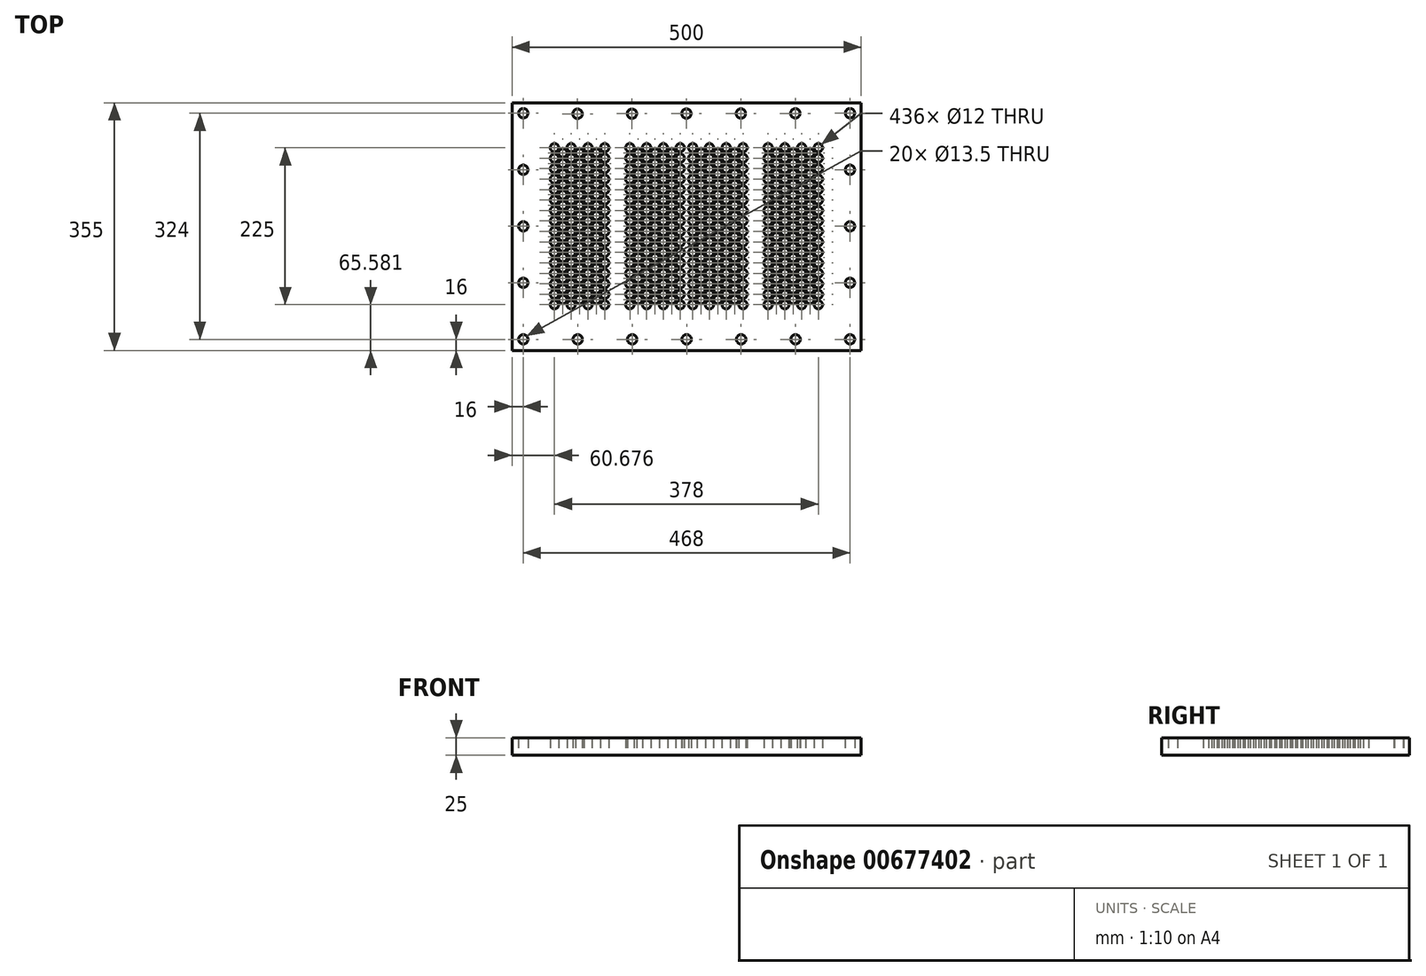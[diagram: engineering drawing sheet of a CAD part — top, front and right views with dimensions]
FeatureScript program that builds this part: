
annotation { "Feature Type Name" : "Feature", "Feature Type Description" : "" }
export const myFeature = defineFeature(function(context is Context, id is Id, definition is map)
    precondition{}
    {
        {
            var Q0;
            Q0=qCreatedBy(makeId("Top.planeOp"),FACE);
            var sketch = newSketch(context, id + "F0", { "sketchPlane" : qUnion([Q0])});
            skLineSegment(sketch, "E0", {"start": v(0, 0) * mm, "end": v(500, 0) * mm});
            skLineSegment(sketch, "E1", {"start": v(500, 0) * mm, "end": v(500, 355) * mm});
            skLineSegment(sketch, "E2", {"start": v(500, 355) * mm, "end": v(0, 355) * mm});
            skLineSegment(sketch, "E3", {"start": v(0, 355) * mm, "end": v(0, 0) * mm});
            skCircle(sketch, "E4", {"center": v(16, 16) * mm, "radius": 6.75 * mm});
            skCircle(sketch, "E5.1.0.0", {"center": v(94, 16) * mm, "radius": 6.75 * mm});
            skCircle(sketch, "E5.2.0.0", {"center": v(172, 16) * mm, "radius": 6.75 * mm});
            skCircle(sketch, "E5.3.0.0", {"center": v(250, 16) * mm, "radius": 6.75 * mm});
            skCircle(sketch, "E5.4.0.0", {"center": v(328, 16) * mm, "radius": 6.75 * mm});
            skCircle(sketch, "E5.5.0.0", {"center": v(406, 16) * mm, "radius": 6.75 * mm});
            skCircle(sketch, "E5.6.0.0", {"center": v(484, 16) * mm, "radius": 6.75 * mm});
            skCircle(sketch, "E6.0.1.0", {"center": v(16, 97) * mm, "radius": 6.75 * mm});
            skCircle(sketch, "E6.0.1.1", {"center": v(484, 97) * mm, "radius": 6.75 * mm});
            skCircle(sketch, "E6.0.2.0", {"center": v(16, 178) * mm, "radius": 6.75 * mm});
            skCircle(sketch, "E6.0.2.1", {"center": v(484, 178) * mm, "radius": 6.75 * mm});
            skCircle(sketch, "E6.0.3.0", {"center": v(16, 259) * mm, "radius": 6.75 * mm});
            skCircle(sketch, "E6.0.3.1", {"center": v(484, 259) * mm, "radius": 6.75 * mm});
            skCircle(sketch, "E6.0.4.0", {"center": v(16, 340) * mm, "radius": 6.75 * mm});
            skCircle(sketch, "E6.0.4.1", {"center": v(484, 340) * mm, "radius": 6.75 * mm});
            skCircle(sketch, "E7.MirrorC", {"center": v(171.68, 339.34) * mm, "radius": 6.75 * mm});
            skCircle(sketch, "E8.MirrorC", {"center": v(93.68, 339.19) * mm, "radius": 6.75 * mm});
            skCircle(sketch, "E9.MirrorC", {"center": v(249.68, 339.5) * mm, "radius": 6.75 * mm});
            skCircle(sketch, "E10.MirrorC", {"center": v(327.68, 339.66) * mm, "radius": 6.75 * mm});
            skCircle(sketch, "E11.MirrorC", {"center": v(405.68, 339.81) * mm, "radius": 6.75 * mm});
            skLineSegment(sketch, "E12", {"start": v(249.68, 355) * mm, "end": v(249.68, 0) * mm, "construction": true});
            skLineSegment(sketch, "E13", {"start": v(0, 177.5) * mm, "end": v(500, 178) * mm, "construction": true});
            skCircle(sketch, "E14.0.1.0", {"center": v(438.68, 80.58) * mm, "radius": 6 * mm});
            skCircle(sketch, "E14.0.2.0", {"center": v(438.68, 95.58) * mm, "radius": 6 * mm});
            skCircle(sketch, "E14.0.3.0", {"center": v(438.68, 110.58) * mm, "radius": 6 * mm});
            skCircle(sketch, "E14.0.4.0", {"center": v(438.68, 125.58) * mm, "radius": 6 * mm});
            skCircle(sketch, "E14.0.5.0", {"center": v(438.68, 140.58) * mm, "radius": 6 * mm});
            skCircle(sketch, "E14.0.6.0", {"center": v(438.68, 155.58) * mm, "radius": 6 * mm});
            skCircle(sketch, "E14.0.7.0", {"center": v(438.68, 170.58) * mm, "radius": 6 * mm});
            skCircle(sketch, "E14.0.8.0", {"center": v(438.68, 185.58) * mm, "radius": 6 * mm});
            skCircle(sketch, "E14.0.9.0", {"center": v(438.68, 200.58) * mm, "radius": 6 * mm});
            skCircle(sketch, "E14.0.10.0", {"center": v(438.68, 215.58) * mm, "radius": 6 * mm});
            skCircle(sketch, "E14.0.11.0", {"center": v(438.68, 230.58) * mm, "radius": 6 * mm});
            skCircle(sketch, "E14.0.12.0", {"center": v(438.68, 245.58) * mm, "radius": 6 * mm});
            skCircle(sketch, "E14.0.13.0", {"center": v(438.68, 260.58) * mm, "radius": 6 * mm});
            skCircle(sketch, "E14.0.14.0", {"center": v(438.68, 275.58) * mm, "radius": 6 * mm});
            skCircle(sketch, "E14.0.15.0", {"center": v(438.68, 290.58) * mm, "radius": 6 * mm});
            skCircle(sketch, "E15.0.1.0", {"center": v(438.67, 65.58) * mm, "radius": 6 * mm});
            skCircle(sketch, "E16.1.0.0", {"center": v(414.68, 200.58) * mm, "radius": 6 * mm});
            skCircle(sketch, "E16.1.0.1", {"center": v(414.68, 185.58) * mm, "radius": 6 * mm});
            skCircle(sketch, "E16.1.0.2", {"center": v(414.68, 170.58) * mm, "radius": 6 * mm});
            skCircle(sketch, "E16.1.0.3", {"center": v(414.68, 155.58) * mm, "radius": 6 * mm});
            skCircle(sketch, "E16.1.0.4", {"center": v(414.68, 140.58) * mm, "radius": 6 * mm});
            skCircle(sketch, "E16.1.0.5", {"center": v(414.68, 110.58) * mm, "radius": 6 * mm});
            skCircle(sketch, "E16.1.0.6", {"center": v(414.68, 125.58) * mm, "radius": 6 * mm});
            skCircle(sketch, "E16.1.0.7", {"center": v(414.68, 95.58) * mm, "radius": 6 * mm});
            skCircle(sketch, "E16.1.0.8", {"center": v(414.68, 80.58) * mm, "radius": 6 * mm});
            skCircle(sketch, "E16.1.0.9", {"center": v(414.68, 65.58) * mm, "radius": 6 * mm});
            skCircle(sketch, "E16.1.0.10", {"center": v(414.68, 290.58) * mm, "radius": 6 * mm});
            skCircle(sketch, "E16.1.0.11", {"center": v(414.68, 275.58) * mm, "radius": 6 * mm});
            skCircle(sketch, "E16.1.0.12", {"center": v(414.68, 260.58) * mm, "radius": 6 * mm});
            skCircle(sketch, "E16.1.0.13", {"center": v(414.68, 245.58) * mm, "radius": 6 * mm});
            skCircle(sketch, "E16.1.0.14", {"center": v(414.68, 230.58) * mm, "radius": 6 * mm});
            skCircle(sketch, "E16.1.0.15", {"center": v(414.68, 215.58) * mm, "radius": 6 * mm});
            skCircle(sketch, "E16.2.0.0", {"center": v(390.68, 200.58) * mm, "radius": 6 * mm});
            skCircle(sketch, "E16.2.0.1", {"center": v(390.68, 185.58) * mm, "radius": 6 * mm});
            skCircle(sketch, "E16.2.0.2", {"center": v(390.68, 170.58) * mm, "radius": 6 * mm});
            skCircle(sketch, "E16.2.0.3", {"center": v(390.68, 155.58) * mm, "radius": 6 * mm});
            skCircle(sketch, "E16.2.0.4", {"center": v(390.68, 140.58) * mm, "radius": 6 * mm});
            skCircle(sketch, "E16.2.0.5", {"center": v(390.68, 110.58) * mm, "radius": 6 * mm});
            skCircle(sketch, "E16.2.0.6", {"center": v(390.68, 125.58) * mm, "radius": 6 * mm});
            skCircle(sketch, "E16.2.0.7", {"center": v(390.68, 95.58) * mm, "radius": 6 * mm});
            skCircle(sketch, "E16.2.0.8", {"center": v(390.68, 80.58) * mm, "radius": 6 * mm});
            skCircle(sketch, "E16.2.0.9", {"center": v(390.68, 65.58) * mm, "radius": 6 * mm});
            skCircle(sketch, "E16.2.0.10", {"center": v(390.68, 290.58) * mm, "radius": 6 * mm});
            skCircle(sketch, "E16.2.0.11", {"center": v(390.68, 275.58) * mm, "radius": 6 * mm});
            skCircle(sketch, "E16.2.0.12", {"center": v(390.68, 260.58) * mm, "radius": 6 * mm});
            skCircle(sketch, "E16.2.0.13", {"center": v(390.68, 245.58) * mm, "radius": 6 * mm});
            skCircle(sketch, "E16.2.0.14", {"center": v(390.68, 230.58) * mm, "radius": 6 * mm});
            skCircle(sketch, "E16.2.0.15", {"center": v(390.68, 215.58) * mm, "radius": 6 * mm});
            skCircle(sketch, "E16.3.0.0", {"center": v(366.68, 200.58) * mm, "radius": 6 * mm});
            skCircle(sketch, "E16.3.0.1", {"center": v(366.68, 185.58) * mm, "radius": 6 * mm});
            skCircle(sketch, "E16.3.0.2", {"center": v(366.68, 170.58) * mm, "radius": 6 * mm});
            skCircle(sketch, "E16.3.0.3", {"center": v(366.68, 155.58) * mm, "radius": 6 * mm});
            skCircle(sketch, "E16.3.0.4", {"center": v(366.68, 140.58) * mm, "radius": 6 * mm});
            skCircle(sketch, "E16.3.0.5", {"center": v(366.68, 110.58) * mm, "radius": 6 * mm});
            skCircle(sketch, "E16.3.0.6", {"center": v(366.68, 125.58) * mm, "radius": 6 * mm});
            skCircle(sketch, "E16.3.0.7", {"center": v(366.68, 95.58) * mm, "radius": 6 * mm});
            skCircle(sketch, "E16.3.0.8", {"center": v(366.68, 80.58) * mm, "radius": 6 * mm});
            skCircle(sketch, "E16.3.0.9", {"center": v(366.68, 65.58) * mm, "radius": 6 * mm});
            skCircle(sketch, "E16.3.0.10", {"center": v(366.68, 290.58) * mm, "radius": 6 * mm});
            skCircle(sketch, "E16.3.0.11", {"center": v(366.68, 275.58) * mm, "radius": 6 * mm});
            skCircle(sketch, "E16.3.0.12", {"center": v(366.68, 260.58) * mm, "radius": 6 * mm});
            skCircle(sketch, "E16.3.0.13", {"center": v(366.68, 245.58) * mm, "radius": 6 * mm});
            skCircle(sketch, "E16.3.0.14", {"center": v(366.68, 230.58) * mm, "radius": 6 * mm});
            skCircle(sketch, "E16.3.0.15", {"center": v(366.68, 215.58) * mm, "radius": 6 * mm});
            skCircle(sketch, "E17", {"center": v(426.68, 73.08) * mm, "radius": 6 * mm});
            skCircle(sketch, "E18.0.1.0", {"center": v(426.68, 88.08) * mm, "radius": 6 * mm});
            skCircle(sketch, "E18.0.2.0", {"center": v(426.68, 103.08) * mm, "radius": 6 * mm});
            skCircle(sketch, "E18.0.3.0", {"center": v(426.68, 118.08) * mm, "radius": 6 * mm});
            skCircle(sketch, "E18.0.4.0", {"center": v(426.68, 133.08) * mm, "radius": 6 * mm});
            skCircle(sketch, "E18.0.5.0", {"center": v(426.68, 148.08) * mm, "radius": 6 * mm});
            skCircle(sketch, "E18.0.6.0", {"center": v(426.68, 163.08) * mm, "radius": 6 * mm});
            skCircle(sketch, "E18.0.7.0", {"center": v(426.68, 178.08) * mm, "radius": 6 * mm});
            skCircle(sketch, "E18.0.8.0", {"center": v(426.68, 193.08) * mm, "radius": 6 * mm});
            skCircle(sketch, "E18.0.9.0", {"center": v(426.68, 208.08) * mm, "radius": 6 * mm});
            skCircle(sketch, "E18.0.10.0", {"center": v(426.68, 223.08) * mm, "radius": 6 * mm});
            skCircle(sketch, "E18.0.11.0", {"center": v(426.68, 238.08) * mm, "radius": 6 * mm});
            skCircle(sketch, "E18.0.12.0", {"center": v(426.68, 253.08) * mm, "radius": 6 * mm});
            skCircle(sketch, "E18.0.13.0", {"center": v(426.68, 268.08) * mm, "radius": 6 * mm});
            skCircle(sketch, "E18.0.14.0", {"center": v(426.68, 283.08) * mm, "radius": 6 * mm});
            skCircle(sketch, "E18.1.0.0", {"center": v(402.68, 73.08) * mm, "radius": 6 * mm});
            skCircle(sketch, "E18.1.1.0", {"center": v(402.68, 88.08) * mm, "radius": 6 * mm});
            skCircle(sketch, "E18.1.2.0", {"center": v(402.68, 103.08) * mm, "radius": 6 * mm});
            skCircle(sketch, "E18.1.3.0", {"center": v(402.68, 118.08) * mm, "radius": 6 * mm});
            skCircle(sketch, "E18.1.4.0", {"center": v(402.68, 133.08) * mm, "radius": 6 * mm});
            skCircle(sketch, "E18.1.5.0", {"center": v(402.68, 148.08) * mm, "radius": 6 * mm});
            skCircle(sketch, "E18.1.6.0", {"center": v(402.68, 163.08) * mm, "radius": 6 * mm});
            skCircle(sketch, "E18.1.7.0", {"center": v(402.68, 178.08) * mm, "radius": 6 * mm});
            skCircle(sketch, "E18.1.8.0", {"center": v(402.68, 193.08) * mm, "radius": 6 * mm});
            skCircle(sketch, "E18.1.9.0", {"center": v(402.68, 208.08) * mm, "radius": 6 * mm});
            skCircle(sketch, "E18.1.10.0", {"center": v(402.68, 223.08) * mm, "radius": 6 * mm});
            skCircle(sketch, "E18.1.11.0", {"center": v(402.68, 238.08) * mm, "radius": 6 * mm});
            skCircle(sketch, "E18.1.12.0", {"center": v(402.68, 253.08) * mm, "radius": 6 * mm});
            skCircle(sketch, "E18.1.13.0", {"center": v(402.68, 268.08) * mm, "radius": 6 * mm});
            skCircle(sketch, "E18.1.14.0", {"center": v(402.68, 283.08) * mm, "radius": 6 * mm});
            skCircle(sketch, "E18.2.0.0", {"center": v(378.68, 73.08) * mm, "radius": 6 * mm});
            skCircle(sketch, "E18.2.1.0", {"center": v(378.68, 88.08) * mm, "radius": 6 * mm});
            skCircle(sketch, "E18.2.2.0", {"center": v(378.68, 103.08) * mm, "radius": 6 * mm});
            skCircle(sketch, "E18.2.3.0", {"center": v(378.68, 118.08) * mm, "radius": 6 * mm});
            skCircle(sketch, "E18.2.4.0", {"center": v(378.68, 133.08) * mm, "radius": 6 * mm});
            skCircle(sketch, "E18.2.5.0", {"center": v(378.68, 148.08) * mm, "radius": 6 * mm});
            skCircle(sketch, "E18.2.6.0", {"center": v(378.68, 163.08) * mm, "radius": 6 * mm});
            skCircle(sketch, "E18.2.7.0", {"center": v(378.68, 178.08) * mm, "radius": 6 * mm});
            skCircle(sketch, "E18.2.8.0", {"center": v(378.68, 193.08) * mm, "radius": 6 * mm});
            skCircle(sketch, "E18.2.9.0", {"center": v(378.68, 208.08) * mm, "radius": 6 * mm});
            skCircle(sketch, "E18.2.10.0", {"center": v(378.68, 223.08) * mm, "radius": 6 * mm});
            skCircle(sketch, "E18.2.11.0", {"center": v(378.68, 238.08) * mm, "radius": 6 * mm});
            skCircle(sketch, "E18.2.12.0", {"center": v(378.68, 253.08) * mm, "radius": 6 * mm});
            skCircle(sketch, "E18.2.13.0", {"center": v(378.68, 268.08) * mm, "radius": 6 * mm});
            skCircle(sketch, "E18.2.14.0", {"center": v(378.68, 283.08) * mm, "radius": 6 * mm});
            skCircle(sketch, "E19.1.0.0", {"center": v(258.68, 65.58) * mm, "radius": 6 * mm});
            skCircle(sketch, "E19.1.0.1", {"center": v(282.68, 65.58) * mm, "radius": 6 * mm});
            skCircle(sketch, "E19.1.0.2", {"center": v(306.68, 65.58) * mm, "radius": 6 * mm});
            skCircle(sketch, "E19.1.0.3", {"center": v(330.68, 215.58) * mm, "radius": 6 * mm});
            skCircle(sketch, "E19.1.0.4", {"center": v(270.68, 238.08) * mm, "radius": 6 * mm});
            skCircle(sketch, "E19.1.0.5", {"center": v(294.68, 223.08) * mm, "radius": 6 * mm});
            skCircle(sketch, "E19.1.0.6", {"center": v(318.68, 208.08) * mm, "radius": 6 * mm});
            skCircle(sketch, "E19.1.0.7", {"center": v(258.68, 290.58) * mm, "radius": 6 * mm});
            skCircle(sketch, "E19.1.0.8", {"center": v(282.68, 290.58) * mm, "radius": 6 * mm});
            skCircle(sketch, "E19.1.0.9", {"center": v(306.68, 290.58) * mm, "radius": 6 * mm});
            skCircle(sketch, "E19.1.0.10", {"center": v(330.68, 230.58) * mm, "radius": 6 * mm});
            skCircle(sketch, "E19.1.0.11", {"center": v(270.68, 253.08) * mm, "radius": 6 * mm});
            skCircle(sketch, "E19.1.0.12", {"center": v(294.68, 238.08) * mm, "radius": 6 * mm});
            skCircle(sketch, "E19.1.0.13", {"center": v(318.68, 223.08) * mm, "radius": 6 * mm});
            skCircle(sketch, "E19.1.0.14", {"center": v(258.68, 275.58) * mm, "radius": 6 * mm});
            skCircle(sketch, "E19.1.0.15", {"center": v(282.68, 275.58) * mm, "radius": 6 * mm});
            skCircle(sketch, "E19.1.0.16", {"center": v(306.68, 275.58) * mm, "radius": 6 * mm});
            skCircle(sketch, "E19.1.0.17", {"center": v(330.68, 245.58) * mm, "radius": 6 * mm});
            skCircle(sketch, "E19.1.0.18", {"center": v(270.68, 268.08) * mm, "radius": 6 * mm});
            skCircle(sketch, "E19.1.0.19", {"center": v(294.68, 253.08) * mm, "radius": 6 * mm});
            skCircle(sketch, "E19.1.0.20", {"center": v(318.68, 238.08) * mm, "radius": 6 * mm});
            skCircle(sketch, "E19.1.0.21", {"center": v(258.68, 260.58) * mm, "radius": 6 * mm});
            skCircle(sketch, "E19.1.0.22", {"center": v(282.68, 260.58) * mm, "radius": 6 * mm});
            skCircle(sketch, "E19.1.0.23", {"center": v(306.68, 260.58) * mm, "radius": 6 * mm});
            skCircle(sketch, "E19.1.0.24", {"center": v(330.68, 260.58) * mm, "radius": 6 * mm});
            skCircle(sketch, "E19.1.0.25", {"center": v(270.68, 283.08) * mm, "radius": 6 * mm});
            skCircle(sketch, "E19.1.0.26", {"center": v(294.68, 268.08) * mm, "radius": 6 * mm});
            skCircle(sketch, "E19.1.0.27", {"center": v(318.68, 253.08) * mm, "radius": 6 * mm});
            skCircle(sketch, "E19.1.0.28", {"center": v(306.68, 245.58) * mm, "radius": 6 * mm});
            skCircle(sketch, "E19.1.0.29", {"center": v(330.68, 275.58) * mm, "radius": 6 * mm});
            skCircle(sketch, "E19.1.0.30", {"center": v(318.68, 268.08) * mm, "radius": 6 * mm});
            skCircle(sketch, "E19.1.0.31", {"center": v(294.68, 283.08) * mm, "radius": 6 * mm});
            skCircle(sketch, "E19.1.0.32", {"center": v(258.68, 245.58) * mm, "radius": 6 * mm});
            skCircle(sketch, "E19.1.0.33", {"center": v(282.68, 245.58) * mm, "radius": 6 * mm});
            skCircle(sketch, "E19.1.0.34", {"center": v(306.68, 230.58) * mm, "radius": 6 * mm});
            skCircle(sketch, "E19.1.0.35", {"center": v(330.68, 290.58) * mm, "radius": 6 * mm});
            skCircle(sketch, "E19.1.0.36", {"center": v(270.68, 73.08) * mm, "radius": 6 * mm});
            skCircle(sketch, "E19.1.0.37", {"center": v(318.68, 283.08) * mm, "radius": 6 * mm});
            skCircle(sketch, "E19.1.0.38", {"center": v(258.68, 230.58) * mm, "radius": 6 * mm});
            skCircle(sketch, "E19.1.0.39", {"center": v(282.68, 230.58) * mm, "radius": 6 * mm});
            skCircle(sketch, "E19.1.0.40", {"center": v(294.68, 118.08) * mm, "radius": 6 * mm});
            skCircle(sketch, "E19.1.0.41", {"center": v(306.68, 140.58) * mm, "radius": 6 * mm});
            skCircle(sketch, "E19.1.0.42", {"center": v(282.68, 140.58) * mm, "radius": 6 * mm});
            skCircle(sketch, "E19.1.0.43", {"center": v(330.68, 140.58) * mm, "radius": 6 * mm});
            skCircle(sketch, "E19.1.0.44", {"center": v(270.68, 163.08) * mm, "radius": 6 * mm});
            skCircle(sketch, "E19.1.0.45", {"center": v(294.68, 148.08) * mm, "radius": 6 * mm});
            skCircle(sketch, "E19.1.0.46", {"center": v(306.68, 215.58) * mm, "radius": 6 * mm});
            skCircle(sketch, "E19.1.0.47", {"center": v(318.68, 133.08) * mm, "radius": 6 * mm});
            skCircle(sketch, "E19.1.0.48", {"center": v(330.67, 65.58) * mm, "radius": 6 * mm});
            skCircle(sketch, "E19.1.0.49", {"center": v(270.68, 88.08) * mm, "radius": 6 * mm});
            skCircle(sketch, "E19.1.0.50", {"center": v(294.68, 73.08) * mm, "radius": 6 * mm});
            skCircle(sketch, "E19.1.0.51", {"center": v(258.68, 215.58) * mm, "radius": 6 * mm});
            skCircle(sketch, "E19.1.0.52", {"center": v(282.68, 215.58) * mm, "radius": 6 * mm});
            skCircle(sketch, "E19.1.0.53", {"center": v(258.68, 110.58) * mm, "radius": 6 * mm});
            skCircle(sketch, "E19.1.0.54", {"center": v(282.68, 110.58) * mm, "radius": 6 * mm});
            skCircle(sketch, "E19.1.0.55", {"center": v(318.68, 103.08) * mm, "radius": 6 * mm});
            skCircle(sketch, "E19.1.0.56", {"center": v(306.68, 110.58) * mm, "radius": 6 * mm});
            skCircle(sketch, "E19.1.0.57", {"center": v(270.68, 178.08) * mm, "radius": 6 * mm});
            skCircle(sketch, "E19.1.0.58", {"center": v(330.68, 155.58) * mm, "radius": 6 * mm});
            skCircle(sketch, "E19.1.0.59", {"center": v(294.68, 163.08) * mm, "radius": 6 * mm});
            skCircle(sketch, "E19.1.0.60", {"center": v(318.68, 148.08) * mm, "radius": 6 * mm});
            skCircle(sketch, "E19.1.0.61", {"center": v(282.68, 200.58) * mm, "radius": 6 * mm});
            skCircle(sketch, "E19.1.0.62", {"center": v(330.68, 80.58) * mm, "radius": 6 * mm});
            skCircle(sketch, "E19.1.0.63", {"center": v(306.68, 200.58) * mm, "radius": 6 * mm});
            skCircle(sketch, "E19.1.0.64", {"center": v(270.68, 103.08) * mm, "radius": 6 * mm});
            skCircle(sketch, "E19.1.0.65", {"center": v(294.68, 88.08) * mm, "radius": 6 * mm});
            skCircle(sketch, "E19.1.0.66", {"center": v(318.68, 73.08) * mm, "radius": 6 * mm});
            skCircle(sketch, "E19.1.0.67", {"center": v(258.68, 200.58) * mm, "radius": 6 * mm});
            skCircle(sketch, "E19.1.0.68", {"center": v(270.68, 193.08) * mm, "radius": 6 * mm});
            skCircle(sketch, "E19.1.0.69", {"center": v(294.68, 178.08) * mm, "radius": 6 * mm});
            skCircle(sketch, "E19.1.0.70", {"center": v(318.68, 163.08) * mm, "radius": 6 * mm});
            skCircle(sketch, "E19.1.0.71", {"center": v(258.68, 170.58) * mm, "radius": 6 * mm});
            skCircle(sketch, "E19.1.0.72", {"center": v(270.68, 133.08) * mm, "radius": 6 * mm});
            skCircle(sketch, "E19.1.0.73", {"center": v(270.68, 223.08) * mm, "radius": 6 * mm});
            skCircle(sketch, "E19.1.0.74", {"center": v(258.68, 140.58) * mm, "radius": 6 * mm});
            skCircle(sketch, "E19.1.0.75", {"center": v(282.68, 170.58) * mm, "radius": 6 * mm});
            skCircle(sketch, "E19.1.0.76", {"center": v(330.68, 200.58) * mm, "radius": 6 * mm});
            skCircle(sketch, "E19.1.0.77", {"center": v(306.68, 80.58) * mm, "radius": 6 * mm});
            skCircle(sketch, "E19.1.0.78", {"center": v(282.68, 80.58) * mm, "radius": 6 * mm});
            skCircle(sketch, "E19.1.0.79", {"center": v(258.68, 80.58) * mm, "radius": 6 * mm});
            skCircle(sketch, "E19.1.0.80", {"center": v(318.68, 118.08) * mm, "radius": 6 * mm});
            skCircle(sketch, "E19.1.0.81", {"center": v(294.68, 133.08) * mm, "radius": 6 * mm});
            skCircle(sketch, "E19.1.0.82", {"center": v(270.68, 148.08) * mm, "radius": 6 * mm});
            skCircle(sketch, "E19.1.0.83", {"center": v(330.68, 125.58) * mm, "radius": 6 * mm});
            skCircle(sketch, "E19.1.0.84", {"center": v(306.68, 155.58) * mm, "radius": 6 * mm});
            skCircle(sketch, "E19.1.0.85", {"center": v(282.68, 155.58) * mm, "radius": 6 * mm});
            skCircle(sketch, "E19.1.0.86", {"center": v(258.68, 155.58) * mm, "radius": 6 * mm});
            skCircle(sketch, "E19.1.0.87", {"center": v(318.68, 178.08) * mm, "radius": 6 * mm});
            skCircle(sketch, "E19.1.0.88", {"center": v(294.68, 193.08) * mm, "radius": 6 * mm});
            skCircle(sketch, "E19.1.0.89", {"center": v(270.68, 208.08) * mm, "radius": 6 * mm});
            skCircle(sketch, "E19.1.0.90", {"center": v(306.68, 95.58) * mm, "radius": 6 * mm});
            skCircle(sketch, "E19.1.0.91", {"center": v(330.68, 185.58) * mm, "radius": 6 * mm});
            skCircle(sketch, "E19.1.0.92", {"center": v(318.68, 88.08) * mm, "radius": 6 * mm});
            skCircle(sketch, "E19.1.0.93", {"center": v(294.68, 103.08) * mm, "radius": 6 * mm});
            skCircle(sketch, "E19.1.0.94", {"center": v(258.68, 185.58) * mm, "radius": 6 * mm});
            skCircle(sketch, "E19.1.0.95", {"center": v(282.68, 95.58) * mm, "radius": 6 * mm});
            skCircle(sketch, "E19.1.0.96", {"center": v(258.68, 95.58) * mm, "radius": 6 * mm});
            skCircle(sketch, "E19.1.0.97", {"center": v(330.68, 170.58) * mm, "radius": 6 * mm});
            skCircle(sketch, "E19.1.0.98", {"center": v(306.68, 125.58) * mm, "radius": 6 * mm});
            skCircle(sketch, "E19.1.0.99", {"center": v(282.68, 185.58) * mm, "radius": 6 * mm});
            skCircle(sketch, "E19.1.0.100", {"center": v(318.68, 193.08) * mm, "radius": 6 * mm});
            skCircle(sketch, "E19.1.0.101", {"center": v(294.68, 208.08) * mm, "radius": 6 * mm});
            skCircle(sketch, "E19.1.0.102", {"center": v(330.68, 110.58) * mm, "radius": 6 * mm});
            skCircle(sketch, "E19.1.0.103", {"center": v(306.68, 170.58) * mm, "radius": 6 * mm});
            skCircle(sketch, "E19.1.0.104", {"center": v(270.68, 118.08) * mm, "radius": 6 * mm});
            skCircle(sketch, "E19.1.0.105", {"center": v(330.68, 95.58) * mm, "radius": 6 * mm});
            skCircle(sketch, "E19.1.0.106", {"center": v(282.68, 125.58) * mm, "radius": 6 * mm});
            skCircle(sketch, "E19.1.0.107", {"center": v(306.68, 185.58) * mm, "radius": 6 * mm});
            skCircle(sketch, "E19.1.0.108", {"center": v(258.68, 125.58) * mm, "radius": 6 * mm});
            skCircle(sketch, "E20.MirrorC", {"center": v(240.68, 185.58) * mm, "radius": 6 * mm});
            skCircle(sketch, "E21.MirrorC", {"center": v(240.68, 80.58) * mm, "radius": 6 * mm});
            skCircle(sketch, "E22.MirrorC", {"center": v(108.68, 65.58) * mm, "radius": 6 * mm});
            skCircle(sketch, "E23.MirrorC", {"center": v(72.68, 178.08) * mm, "radius": 6 * mm});
            skCircle(sketch, "E24.MirrorC", {"center": v(96.68, 193.08) * mm, "radius": 6 * mm});
            skCircle(sketch, "E25.MirrorC", {"center": v(204.68, 238.08) * mm, "radius": 6 * mm});
            skCircle(sketch, "E26.MirrorC", {"center": v(204.68, 163.08) * mm, "radius": 6 * mm});
            skCircle(sketch, "E27.MirrorC", {"center": v(168.68, 80.58) * mm, "radius": 6 * mm});
            skCircle(sketch, "E28.MirrorC", {"center": v(216.68, 80.58) * mm, "radius": 6 * mm});
            skCircle(sketch, "E29.MirrorC", {"center": v(180.68, 253.08) * mm, "radius": 6 * mm});
            skCircle(sketch, "E30.MirrorC", {"center": v(60.68, 185.58) * mm, "radius": 6 * mm});
            skCircle(sketch, "E31.MirrorC", {"center": v(168.68, 230.58) * mm, "radius": 6 * mm});
            skCircle(sketch, "E32.MirrorC", {"center": v(72.68, 238.08) * mm, "radius": 6 * mm});
            skCircle(sketch, "E33.MirrorC", {"center": v(120.68, 208.08) * mm, "radius": 6 * mm});
            skCircle(sketch, "E34.MirrorC", {"center": v(60.68, 80.58) * mm, "radius": 6 * mm});
            skCircle(sketch, "E35.MirrorC", {"center": v(192.68, 185.58) * mm, "radius": 6 * mm});
            skCircle(sketch, "E36.MirrorC", {"center": v(168.68, 185.58) * mm, "radius": 6 * mm});
            skCircle(sketch, "E37.MirrorC", {"center": v(96.68, 253.08) * mm, "radius": 6 * mm});
            skCircle(sketch, "E38.MirrorC", {"center": v(120.68, 268.08) * mm, "radius": 6 * mm});
            skCircle(sketch, "E39.MirrorC", {"center": v(228.68, 253.08) * mm, "radius": 6 * mm});
            skCircle(sketch, "E40.MirrorC", {"center": v(240.68, 275.58) * mm, "radius": 6 * mm});
            skCircle(sketch, "E41.MirrorC", {"center": v(60.68, 245.58) * mm, "radius": 6 * mm});
            skCircle(sketch, "E42.MirrorC", {"center": v(84.68, 275.58) * mm, "radius": 6 * mm});
            skCircle(sketch, "E43.MirrorC", {"center": v(72.68, 193.08) * mm, "radius": 6 * mm});
            skCircle(sketch, "E44.MirrorC", {"center": v(108.68, 275.58) * mm, "radius": 6 * mm});
            skCircle(sketch, "E45.MirrorC", {"center": v(216.68, 170.58) * mm, "radius": 6 * mm});
            skCircle(sketch, "E46.MirrorC", {"center": v(168.68, 140.58) * mm, "radius": 6 * mm});
            skCircle(sketch, "E47.MirrorC", {"center": v(180.68, 268.08) * mm, "radius": 6 * mm});
            skCircle(sketch, "E48.MirrorC", {"center": v(204.68, 103.08) * mm, "radius": 6 * mm});
            skCircle(sketch, "E49.MirrorC", {"center": v(168.68, 275.58) * mm, "radius": 6 * mm});
            skCircle(sketch, "E50.MirrorC", {"center": v(204.68, 148.08) * mm, "radius": 6 * mm});
            skCircle(sketch, "E51.MirrorC", {"center": v(216.68, 200.58) * mm, "radius": 6 * mm});
            skCircle(sketch, "E52.MirrorC", {"center": v(72.68, 73.08) * mm, "radius": 6 * mm});
            skCircle(sketch, "E53.MirrorC", {"center": v(192.68, 80.58) * mm, "radius": 6 * mm});
            skCircle(sketch, "E54.MirrorC", {"center": v(216.68, 125.58) * mm, "radius": 6 * mm});
            skCircle(sketch, "E55.MirrorC", {"center": v(204.68, 268.08) * mm, "radius": 6 * mm});
            skCircle(sketch, "E56.MirrorC", {"center": v(216.68, 140.58) * mm, "radius": 6 * mm});
            skCircle(sketch, "E57.MirrorC", {"center": v(96.68, 238.08) * mm, "radius": 6 * mm});
            skCircle(sketch, "E58.MirrorC", {"center": v(168.68, 155.58) * mm, "radius": 6 * mm});
            skCircle(sketch, "E59.MirrorC", {"center": v(240.68, 140.58) * mm, "radius": 6 * mm});
            skCircle(sketch, "E60.MirrorC", {"center": v(204.68, 193.08) * mm, "radius": 6 * mm});
            skCircle(sketch, "E61.MirrorC", {"center": v(168.68, 260.58) * mm, "radius": 6 * mm});
            skCircle(sketch, "E62.MirrorC", {"center": v(120.68, 253.08) * mm, "radius": 6 * mm});
            skCircle(sketch, "E63.MirrorC", {"center": v(228.68, 118.08) * mm, "radius": 6 * mm});
            skCircle(sketch, "E64.MirrorC", {"center": v(204.68, 118.08) * mm, "radius": 6 * mm});
            skCircle(sketch, "E65.MirrorC", {"center": v(228.68, 133.08) * mm, "radius": 6 * mm});
            skCircle(sketch, "E66.MirrorC", {"center": v(192.68, 110.58) * mm, "radius": 6 * mm});
            skCircle(sketch, "E67.MirrorC", {"center": v(72.68, 148.08) * mm, "radius": 6 * mm});
            skCircle(sketch, "E68.MirrorC", {"center": v(96.68, 163.08) * mm, "radius": 6 * mm});
            skCircle(sketch, "E69.MirrorC", {"center": v(60.68, 170.58) * mm, "radius": 6 * mm});
            skCircle(sketch, "E70.MirrorC", {"center": v(60.68, 155.58) * mm, "radius": 6 * mm});
            skCircle(sketch, "E71.MirrorC", {"center": v(120.68, 178.08) * mm, "radius": 6 * mm});
            skCircle(sketch, "E72.MirrorC", {"center": v(84.68, 125.58) * mm, "radius": 6 * mm});
            skCircle(sketch, "E73.MirrorC", {"center": v(84.68, 110.58) * mm, "radius": 6 * mm});
            skCircle(sketch, "E74.MirrorC", {"center": v(108.68, 110.58) * mm, "radius": 6 * mm});
            skCircle(sketch, "E75.MirrorC", {"center": v(108.68, 125.58) * mm, "radius": 6 * mm});
            skCircle(sketch, "E76.MirrorC", {"center": v(180.68, 223.08) * mm, "radius": 6 * mm});
            skCircle(sketch, "E77.MirrorC", {"center": v(60.68, 230.58) * mm, "radius": 6 * mm});
            skCircle(sketch, "E78.MirrorC", {"center": v(120.68, 238.08) * mm, "radius": 6 * mm});
            skCircle(sketch, "E79.MirrorC", {"center": v(180.68, 178.08) * mm, "radius": 6 * mm});
            skCircle(sketch, "E80.MirrorC", {"center": v(192.68, 170.58) * mm, "radius": 6 * mm});
            skCircle(sketch, "E81.MirrorC", {"center": v(192.68, 260.58) * mm, "radius": 6 * mm});
            skCircle(sketch, "E82.MirrorC", {"center": v(216.68, 230.58) * mm, "radius": 6 * mm});
            skCircle(sketch, "E83.MirrorC", {"center": v(192.68, 140.58) * mm, "radius": 6 * mm});
            skCircle(sketch, "E84.MirrorC", {"center": v(204.68, 178.08) * mm, "radius": 6 * mm});
            skCircle(sketch, "E85.MirrorC", {"center": v(240.68, 170.58) * mm, "radius": 6 * mm});
            skCircle(sketch, "E86.MirrorC", {"center": v(72.68, 133.08) * mm, "radius": 6 * mm});
            skCircle(sketch, "E87.MirrorC", {"center": v(228.68, 178.08) * mm, "radius": 6 * mm});
            skCircle(sketch, "E88.MirrorC", {"center": v(228.68, 223.08) * mm, "radius": 6 * mm});
            skCircle(sketch, "E89.MirrorC", {"center": v(96.68, 148.08) * mm, "radius": 6 * mm});
            skCircle(sketch, "E90.MirrorC", {"center": v(72.68, 163.08) * mm, "radius": 6 * mm});
            skCircle(sketch, "E91.MirrorC", {"center": v(120.68, 163.08) * mm, "radius": 6 * mm});
            skCircle(sketch, "E92.MirrorC", {"center": v(96.68, 178.08) * mm, "radius": 6 * mm});
            skCircle(sketch, "E93.MirrorC", {"center": v(60.68, 140.58) * mm, "radius": 6 * mm});
            skCircle(sketch, "E94.MirrorC", {"center": v(120.68, 193.08) * mm, "radius": 6 * mm});
            skCircle(sketch, "E95.MirrorC", {"center": v(84.68, 140.58) * mm, "radius": 6 * mm});
            skCircle(sketch, "E96.MirrorC", {"center": v(108.68, 140.58) * mm, "radius": 6 * mm});
            skCircle(sketch, "E97.MirrorC", {"center": v(216.68, 155.58) * mm, "radius": 6 * mm});
            skCircle(sketch, "E98.MirrorC", {"center": v(204.68, 223.08) * mm, "radius": 6 * mm});
            skCircle(sketch, "E99.MirrorC", {"center": v(240.68, 260.58) * mm, "radius": 6 * mm});
            skCircle(sketch, "E100.MirrorC", {"center": v(240.68, 110.58) * mm, "radius": 6 * mm});
            skCircle(sketch, "E101.MirrorC", {"center": v(120.68, 133.08) * mm, "radius": 6 * mm});
            skCircle(sketch, "E102.MirrorC", {"center": v(96.68, 118.08) * mm, "radius": 6 * mm});
            skCircle(sketch, "E103.MirrorC", {"center": v(60.68, 110.58) * mm, "radius": 6 * mm});
            skCircle(sketch, "E104.MirrorC", {"center": v(84.68, 170.58) * mm, "radius": 6 * mm});
            skCircle(sketch, "E105.MirrorC", {"center": v(108.68, 170.58) * mm, "radius": 6 * mm});
            skCircle(sketch, "E106.MirrorC", {"center": v(240.68, 155.58) * mm, "radius": 6 * mm});
            skCircle(sketch, "E107.MirrorC", {"center": v(168.68, 110.58) * mm, "radius": 6 * mm});
            skCircle(sketch, "E108.MirrorC", {"center": v(216.68, 260.58) * mm, "radius": 6 * mm});
            skCircle(sketch, "E109.MirrorC", {"center": v(240.68, 230.58) * mm, "radius": 6 * mm});
            skCircle(sketch, "E110.MirrorC", {"center": v(216.68, 110.58) * mm, "radius": 6 * mm});
            skCircle(sketch, "E111.MirrorC", {"center": v(180.68, 163.08) * mm, "radius": 6 * mm});
            skCircle(sketch, "E112.MirrorC", {"center": v(72.68, 118.08) * mm, "radius": 6 * mm});
            skCircle(sketch, "E113.MirrorC", {"center": v(96.68, 133.08) * mm, "radius": 6 * mm});
            skCircle(sketch, "E114.MirrorC", {"center": v(120.68, 148.08) * mm, "radius": 6 * mm});
            skCircle(sketch, "E115.MirrorC", {"center": v(60.68, 125.58) * mm, "radius": 6 * mm});
            skCircle(sketch, "E116.MirrorC", {"center": v(72.68, 253.08) * mm, "radius": 6 * mm});
            skCircle(sketch, "E117.MirrorC", {"center": v(84.68, 155.58) * mm, "radius": 6 * mm});
            skCircle(sketch, "E118.MirrorC", {"center": v(108.68, 155.58) * mm, "radius": 6 * mm});
            skCircle(sketch, "E119.MirrorC", {"center": v(96.68, 88.08) * mm, "radius": 6 * mm});
            skCircle(sketch, "E120.MirrorC", {"center": v(228.68, 193.08) * mm, "radius": 6 * mm});
            skCircle(sketch, "E121.MirrorC", {"center": v(192.68, 155.58) * mm, "radius": 6 * mm});
            skCircle(sketch, "E122.MirrorC", {"center": v(228.68, 238.08) * mm, "radius": 6 * mm});
            skCircle(sketch, "E123.MirrorC", {"center": v(180.68, 193.08) * mm, "radius": 6 * mm});
            skCircle(sketch, "E124.MirrorC", {"center": v(180.68, 238.08) * mm, "radius": 6 * mm});
            skCircle(sketch, "E125.MirrorC", {"center": v(228.68, 73.08) * mm, "radius": 6 * mm});
            skCircle(sketch, "E126.MirrorC", {"center": v(72.68, 88.08) * mm, "radius": 6 * mm});
            skCircle(sketch, "E127.MirrorC", {"center": v(120.68, 118.08) * mm, "radius": 6 * mm});
            skCircle(sketch, "E128.MirrorC", {"center": v(84.68, 185.58) * mm, "radius": 6 * mm});
            skCircle(sketch, "E129.MirrorC", {"center": v(108.68, 185.58) * mm, "radius": 6 * mm});
            skCircle(sketch, "E130.MirrorC", {"center": v(168.68, 125.58) * mm, "radius": 6 * mm});
            skCircle(sketch, "E131.MirrorC", {"center": v(216.68, 185.58) * mm, "radius": 6 * mm});
            skCircle(sketch, "E132.MirrorC", {"center": v(204.68, 253.08) * mm, "radius": 6 * mm});
            skCircle(sketch, "E133.MirrorC", {"center": v(180.68, 73.08) * mm, "radius": 6 * mm});
            skCircle(sketch, "E134.MirrorC", {"center": v(192.68, 125.58) * mm, "radius": 6 * mm});
            skCircle(sketch, "E135.MirrorC", {"center": v(228.68, 148.08) * mm, "radius": 6 * mm});
            skCircle(sketch, "E136.MirrorC", {"center": v(192.68, 65.58) * mm, "radius": 6 * mm});
            skCircle(sketch, "E137.MirrorC", {"center": v(228.68, 268.08) * mm, "radius": 6 * mm});
            skCircle(sketch, "E138.MirrorC", {"center": v(192.68, 230.58) * mm, "radius": 6 * mm});
            skCircle(sketch, "E139.MirrorC", {"center": v(204.68, 73.08) * mm, "radius": 6 * mm});
            skCircle(sketch, "E140.MirrorC", {"center": v(120.68, 88.08) * mm, "radius": 6 * mm});
            skCircle(sketch, "E141.MirrorC", {"center": v(60.68, 65.58) * mm, "radius": 6 * mm});
            skCircle(sketch, "E142.MirrorC", {"center": v(96.68, 73.08) * mm, "radius": 6 * mm});
            skCircle(sketch, "E143.MirrorC", {"center": v(204.68, 133.08) * mm, "radius": 6 * mm});
            skCircle(sketch, "E144.MirrorC", {"center": v(216.68, 275.58) * mm, "radius": 6 * mm});
            skCircle(sketch, "E145.MirrorC", {"center": v(168.68, 170.58) * mm, "radius": 6 * mm});
            skCircle(sketch, "E146.MirrorC", {"center": v(180.68, 88.08) * mm, "radius": 6 * mm});
            skCircle(sketch, "E147.MirrorC", {"center": v(240.68, 125.58) * mm, "radius": 6 * mm});
            skCircle(sketch, "E148.MirrorC", {"center": v(216.68, 245.58) * mm, "radius": 6 * mm});
            skCircle(sketch, "E149.MirrorC", {"center": v(168.68, 245.58) * mm, "radius": 6 * mm});
            skCircle(sketch, "E150.MirrorC", {"center": v(108.68, 230.58) * mm, "radius": 6 * mm});
            skCircle(sketch, "E151.MirrorC", {"center": v(120.68, 73.08) * mm, "radius": 6 * mm});
            skCircle(sketch, "E152.MirrorC", {"center": v(84.68, 230.58) * mm, "radius": 6 * mm});
            skCircle(sketch, "E153.MirrorC", {"center": v(192.68, 245.58) * mm, "radius": 6 * mm});
            skCircle(sketch, "E154.MirrorC", {"center": v(228.68, 163.08) * mm, "radius": 6 * mm});
            skCircle(sketch, "E155.MirrorC", {"center": v(228.68, 103.08) * mm, "radius": 6 * mm});
            skCircle(sketch, "E156.MirrorC", {"center": v(120.68, 283.08) * mm, "radius": 6 * mm});
            skCircle(sketch, "E157.MirrorC", {"center": v(180.68, 118.08) * mm, "radius": 6 * mm});
            skCircle(sketch, "E158.MirrorC", {"center": v(240.68, 65.58) * mm, "radius": 6 * mm});
            skCircle(sketch, "E159.MirrorC", {"center": v(240.68, 245.58) * mm, "radius": 6 * mm});
            skCircle(sketch, "E160.MirrorC", {"center": v(168.68, 65.58) * mm, "radius": 6 * mm});
            skCircle(sketch, "E161.MirrorC", {"center": v(192.68, 275.58) * mm, "radius": 6 * mm});
            skCircle(sketch, "E162.MirrorC", {"center": v(96.68, 268.08) * mm, "radius": 6 * mm});
            skCircle(sketch, "E163.MirrorC", {"center": v(180.68, 148.08) * mm, "radius": 6 * mm});
            skCircle(sketch, "E164.MirrorC", {"center": v(168.68, 200.58) * mm, "radius": 6 * mm});
            skCircle(sketch, "E165.MirrorC", {"center": v(108.68, 245.58) * mm, "radius": 6 * mm});
            skCircle(sketch, "E166.MirrorC", {"center": v(72.68, 268.08) * mm, "radius": 6 * mm});
            skCircle(sketch, "E167.MirrorC", {"center": v(60.68, 275.58) * mm, "radius": 6 * mm});
            skCircle(sketch, "E168.MirrorC", {"center": v(84.68, 245.58) * mm, "radius": 6 * mm});
            skCircle(sketch, "E169.MirrorC", {"center": v(72.68, 208.08) * mm, "radius": 6 * mm});
            skCircle(sketch, "E170.MirrorC", {"center": v(180.68, 133.08) * mm, "radius": 6 * mm});
            skCircle(sketch, "E171.MirrorC", {"center": v(60.68, 260.58) * mm, "radius": 6 * mm});
            skCircle(sketch, "E172.MirrorC", {"center": v(84.68, 260.58) * mm, "radius": 6 * mm});
            skCircle(sketch, "E173.MirrorC", {"center": v(108.68, 260.58) * mm, "radius": 6 * mm});
            skCircle(sketch, "E174.MirrorC", {"center": v(96.68, 223.08) * mm, "radius": 6 * mm});
            skCircle(sketch, "E175.MirrorC", {"center": v(84.68, 65.58) * mm, "radius": 6 * mm});
            skCircle(sketch, "E176.MirrorC", {"center": v(60.68, 215.58) * mm, "radius": 6 * mm});
            skCircle(sketch, "E177.MirrorC", {"center": v(108.68, 95.58) * mm, "radius": 6 * mm});
            skCircle(sketch, "E178.MirrorC", {"center": v(60.68, 200.58) * mm, "radius": 6 * mm});
            skCircle(sketch, "E179.MirrorC", {"center": v(84.68, 95.58) * mm, "radius": 6 * mm});
            skCircle(sketch, "E180.MirrorC", {"center": v(132.68, 80.58) * mm, "radius": 6 * mm});
            skCircle(sketch, "E181.MirrorC", {"center": v(108.68, 80.58) * mm, "radius": 6 * mm});
            skCircle(sketch, "E182.MirrorC", {"center": v(84.68, 80.58) * mm, "radius": 6 * mm});
            skCircle(sketch, "E183.MirrorC", {"center": v(120.68, 223.08) * mm, "radius": 6 * mm});
            skCircle(sketch, "E184.MirrorC", {"center": v(96.68, 208.08) * mm, "radius": 6 * mm});
            skCircle(sketch, "E185.MirrorC", {"center": v(132.68, 140.58) * mm, "radius": 6 * mm});
            skCircle(sketch, "E186.MirrorC", {"center": v(132.68, 275.58) * mm, "radius": 6 * mm});
            skCircle(sketch, "E187.MirrorC", {"center": v(72.68, 223.08) * mm, "radius": 6 * mm});
            skCircle(sketch, "E188.MirrorC", {"center": v(132.68, 95.58) * mm, "radius": 6 * mm});
            skCircle(sketch, "E189.MirrorC", {"center": v(192.68, 95.58) * mm, "radius": 6 * mm});
            skCircle(sketch, "E190.MirrorC", {"center": v(216.68, 290.58) * mm, "radius": 6 * mm});
            skCircle(sketch, "E191.MirrorC", {"center": v(132.68, 125.58) * mm, "radius": 6 * mm});
            skCircle(sketch, "E192.MirrorC", {"center": v(132.68, 110.58) * mm, "radius": 6 * mm});
            skCircle(sketch, "E193.MirrorC", {"center": v(120.68, 103.08) * mm, "radius": 6 * mm});
            skCircle(sketch, "E194.MirrorC", {"center": v(84.68, 200.58) * mm, "radius": 6 * mm});
            skCircle(sketch, "E195.MirrorC", {"center": v(84.68, 290.58) * mm, "radius": 6 * mm});
            skCircle(sketch, "E196.MirrorC", {"center": v(108.68, 290.58) * mm, "radius": 6 * mm});
            skCircle(sketch, "E197.MirrorC", {"center": v(132.68, 200.58) * mm, "radius": 6 * mm});
            skCircle(sketch, "E198.MirrorC", {"center": v(228.68, 208.08) * mm, "radius": 6 * mm});
            skCircle(sketch, "E199.MirrorC", {"center": v(168.68, 95.58) * mm, "radius": 6 * mm});
            skCircle(sketch, "E200.MirrorC", {"center": v(228.68, 283.08) * mm, "radius": 6 * mm});
            skCircle(sketch, "E201.MirrorC", {"center": v(180.68, 103.08) * mm, "radius": 6 * mm});
            skCircle(sketch, "E202.MirrorC", {"center": v(132.68, 290.58) * mm, "radius": 6 * mm});
            skCircle(sketch, "E203.MirrorC", {"center": v(240.68, 290.58) * mm, "radius": 6 * mm});
            skCircle(sketch, "E204.MirrorC", {"center": v(192.68, 290.58) * mm, "radius": 6 * mm});
            skCircle(sketch, "E205.MirrorC", {"center": v(108.68, 200.58) * mm, "radius": 6 * mm});
            skCircle(sketch, "E206.MirrorC", {"center": v(204.68, 208.08) * mm, "radius": 6 * mm});
            skCircle(sketch, "E207.MirrorC", {"center": v(180.68, 283.08) * mm, "radius": 6 * mm});
            skCircle(sketch, "E208.MirrorC", {"center": v(132.68, 170.58) * mm, "radius": 6 * mm});
            skCircle(sketch, "E209.MirrorC", {"center": v(72.68, 103.08) * mm, "radius": 6 * mm});
            skCircle(sketch, "E210.MirrorC", {"center": v(192.68, 215.58) * mm, "radius": 6 * mm});
            skCircle(sketch, "E211.MirrorC", {"center": v(180.68, 208.08) * mm, "radius": 6 * mm});
            skCircle(sketch, "E212.MirrorC", {"center": v(132.68, 155.58) * mm, "radius": 6 * mm});
            skCircle(sketch, "E213.MirrorC", {"center": v(132.68, 185.58) * mm, "radius": 6 * mm});
            skCircle(sketch, "E214.MirrorC", {"center": v(216.68, 215.58) * mm, "radius": 6 * mm});
            skCircle(sketch, "E215.MirrorC", {"center": v(96.68, 103.08) * mm, "radius": 6 * mm});
            skCircle(sketch, "E216.MirrorC", {"center": v(60.68, 95.58) * mm, "radius": 6 * mm});
            skCircle(sketch, "E217.MirrorC", {"center": v(240.68, 200.58) * mm, "radius": 6 * mm});
            skCircle(sketch, "E218.MirrorC", {"center": v(168.68, 215.58) * mm, "radius": 6 * mm});
            skCircle(sketch, "E219.MirrorC", {"center": v(168.68, 290.58) * mm, "radius": 6 * mm});
            skCircle(sketch, "E220.MirrorC", {"center": v(240.68, 215.58) * mm, "radius": 6 * mm});
            skCircle(sketch, "E221.MirrorC", {"center": v(108.68, 215.58) * mm, "radius": 6 * mm});
            skCircle(sketch, "E222.MirrorC", {"center": v(132.68, 215.58) * mm, "radius": 6 * mm});
            skCircle(sketch, "E223.MirrorC", {"center": v(84.68, 215.58) * mm, "radius": 6 * mm});
            skCircle(sketch, "E224.MirrorC", {"center": v(204.68, 88.08) * mm, "radius": 6 * mm});
            skCircle(sketch, "E225.MirrorC", {"center": v(216.68, 65.58) * mm, "radius": 6 * mm});
            skCircle(sketch, "E226.MirrorC", {"center": v(228.68, 88.08) * mm, "radius": 6 * mm});
            skCircle(sketch, "E227.MirrorC", {"center": v(132.68, 230.58) * mm, "radius": 6 * mm});
            skCircle(sketch, "E228.MirrorC", {"center": v(72.68, 283.08) * mm, "radius": 6 * mm});
            skCircle(sketch, "E229.MirrorC", {"center": v(60.68, 290.58) * mm, "radius": 6 * mm});
            skCircle(sketch, "E230.MirrorC", {"center": v(240.68, 95.58) * mm, "radius": 6 * mm});
            skCircle(sketch, "E231.MirrorC", {"center": v(132.68, 245.58) * mm, "radius": 6 * mm});
            skCircle(sketch, "E232.MirrorC", {"center": v(96.68, 283.08) * mm, "radius": 6 * mm});
            skCircle(sketch, "E233.MirrorC", {"center": v(216.68, 95.58) * mm, "radius": 6 * mm});
            skCircle(sketch, "E234.MirrorC", {"center": v(204.68, 283.08) * mm, "radius": 6 * mm});
            skCircle(sketch, "E235.MirrorC", {"center": v(192.68, 200.58) * mm, "radius": 6 * mm});
            skCircle(sketch, "E236.MirrorC", {"center": v(132.68, 65.58) * mm, "radius": 6 * mm});
            skCircle(sketch, "E237.MirrorC", {"center": v(132.68, 260.58) * mm, "radius": 6 * mm});
            skSolve(sketch);
        }
        {
            var Q0;
            Q0=makeQuery(id+"F0.imprint","IMPRINT",FACE,{"disambiguationData":[TD([[makeQuery(id+"F0.imprint","IMPRINT",EDGE,{"derivedFrom":sQuery(id+"F0.wireOp",EDGE,"E0")}),1.0]])]});
            extrude(context, id + "F1", {"entities" : qUnion([Q0]), "depth" : 25 * mm, "offsetDistance" : 25 * mm});
        }
    });
